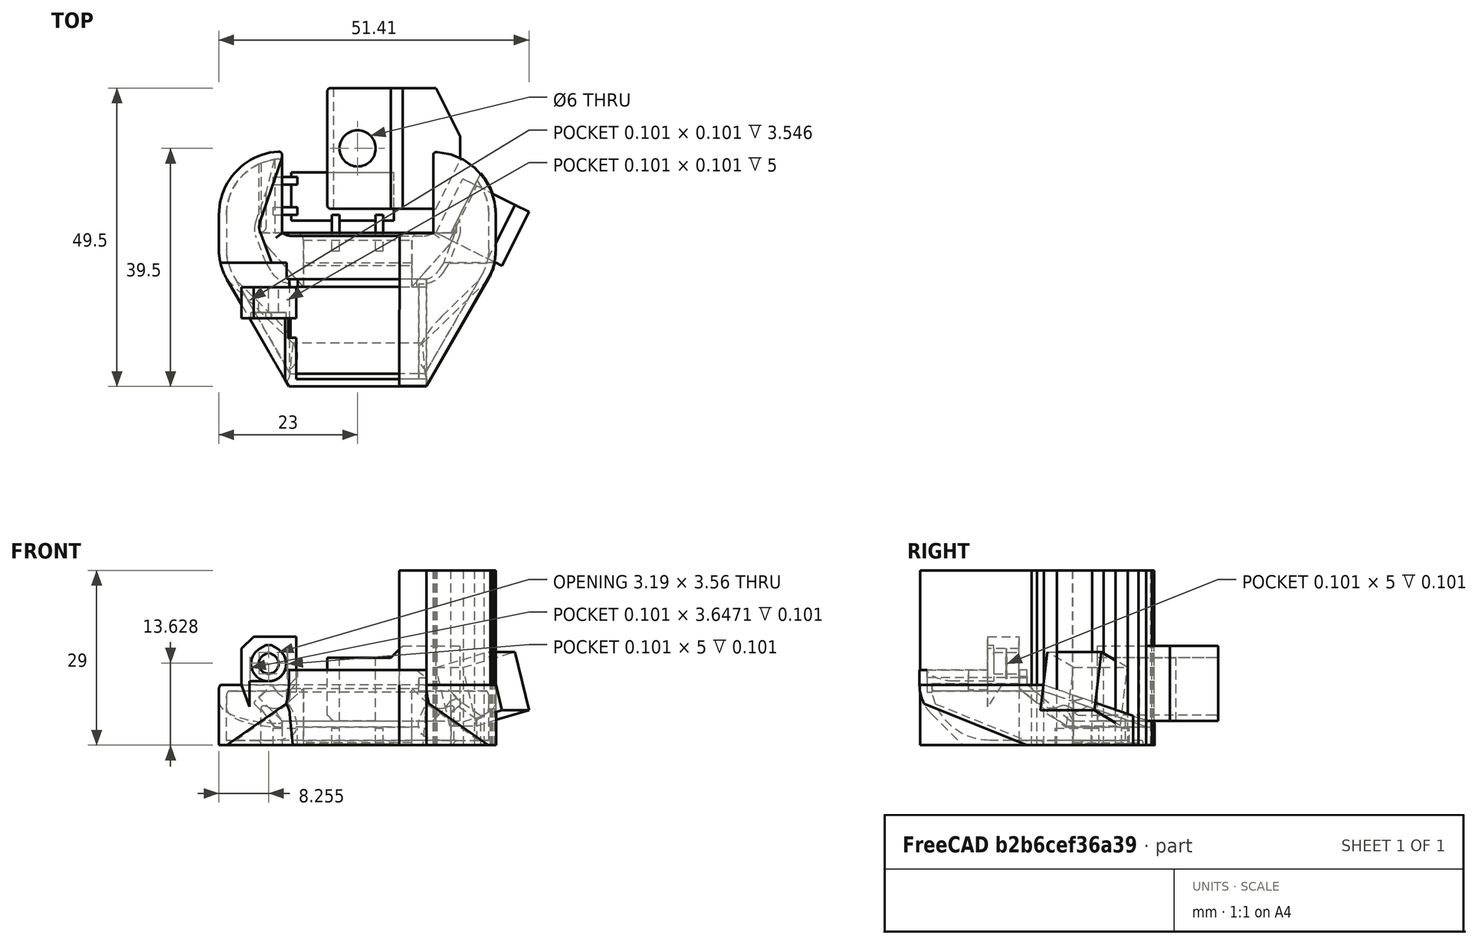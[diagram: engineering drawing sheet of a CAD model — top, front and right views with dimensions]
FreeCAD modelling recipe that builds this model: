
FCSTD DOCUMENT  (FreeCAD 0.18R16146 (Git))
Label: mosquito-duct-lite-mirror-ext
License: All rights reserved
LicenseURL: http://en.wikipedia.org/wiki/All_rights_reserved
objects: Part::Box×7, Part::Feature×4, Part::MultiFuse×2, Part::Cut×1
note: 14 computed .brp shape members not serialized (recipe doc carries the construction recipe); baked Part::Feature solids carry a one-line shape summary decoded from their .brp

FEATURE [Part::Feature] Part__Feature050  label="nozzle_fan_duct"
  Placement = pos=(0.005,14,-6.0794e-11) rot=(0,0,1;0rad)
  shape: bbox 46.01 x 38.99 x 18.01 mm, 128 faces (baked)
FEATURE [Part::Box] Box009  label="Cube009"
  AttacherType = Attacher::AttachEngine3D
  Height = 2.8
  Length = 1.25
  Placement = pos=(3,-3,0) rot=(0,0,1;0rad)
  Width = 6
FEATURE [Part::Box] Box010  label="Cube010"
  AttacherType = Attacher::AttachEngine3D
  Height = 2.8
  Length = 1.25
  Placement = pos=(-4.25,-3,0) rot=(0,0,1;0rad)
  Width = 6
FEATURE [Part::Box] Box011  label="Cube011"
  AttacherType = Attacher::AttachEngine3D
  Height = 2.8
  Length = 4
  Placement = pos=(-14,3,0) rot=(0,0,1;0rad)
  Width = 1.25
FEATURE [Part::Box] Box012  label="Cube012"
  AttacherType = Attacher::AttachEngine3D
  Height = 2.8
  Length = 4
  Placement = pos=(-14,8,0) rot=(0,0,1;0rad)
  Width = 1.25
FEATURE [Part::Box] Box013  label="Cube013"
  AttacherType = Attacher::AttachEngine3D
  Height = 0.2
  Length = 17
  Placement = pos=(-11,2,0) rot=(0,0,1;0rad)
  Width = 8
FEATURE [Part::MultiFuse] Fusion001  label="support"
  Shapes = -> [Box010,Box011,Box009,Box012,Box013]
FEATURE [Part::Feature] Cut001001  label="heat-block"
  Placement = pos=(3e-15,14,4) rot=(0,0,-1;1.5708rad)
  shape: bbox 22 x 20 x 12.5 mm, 14 faces (baked)
FEATURE [Part::Feature] Body002  label="Body-route"
  shape: bbox 16 x 38.8 x 29 mm, 23 faces (baked)
FEATURE [Part::Box] Box016003003018007  label="Cube044"
  AttacherType = Attacher::AttachEngine3D
  Height = 10
  Length = 10
  Placement = pos=(5.5,0,0) rot=(0,0,1;0rad)
  Width = 17
FEATURE [Part::Feature] Box016003003018006001  label="Cube045"
  Placement = pos=(3.05,4.46,0) rot=(0,0,1;0rad)
  shape: bbox 16.53 x 19.68 x 10 mm, 6 faces (baked)
FEATURE [Part::MultiFuse] Fusion003
  Shapes = -> [Box016003003018006001,Box016003003018007]
FEATURE [Part::Cut] Cut
  Base = -> Part__Feature050
  Tool = -> Fusion003
FEATURE [Part::Box] Box  label="Cube"
  AttacherType = Attacher::AttachEngine3D
  Height = 10
  Length = 10
  Placement = pos=(15.3067,-1.15074,3.22595) rot=(0.11416,0.48482,0.867131;5.75288rad)
  Width = 10
